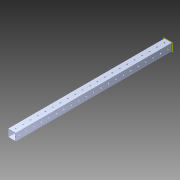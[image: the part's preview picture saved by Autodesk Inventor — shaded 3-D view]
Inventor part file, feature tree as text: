
AUTODESK INVENTOR PART (.ipt)
format: ipt  version: 2014 (Build 180170000, 170)  size: 1,234,432 bytes
history: native  units: in
note: dims shown in document units (in); Inventor stores cm internally (conversion verified against a paired STEP export)
features: pattern_circular x1, other x1, plane x1, extrude x1, imported_body x1, sketch x1
ambient origin geometry x8: Origin, YZ Plane, XZ Plane, XY Plane, X Axis, Y Axis, Z Axis, Center Point
bodies: Body1 (feature_tree)
feature tree (6):
  pattern_circular  "CirPattern2"
  other  "217-3426-STEP1"
  plane  "Work Plane1"
  extrude  "Extrusion1"  Depth=3937.0079in TaperAngle=0.0deg
  imported_body  "Base1"
  sketch  "Sketch1"  dims[d0=-21.0in d1=3937.0079in d2=0.0in]
